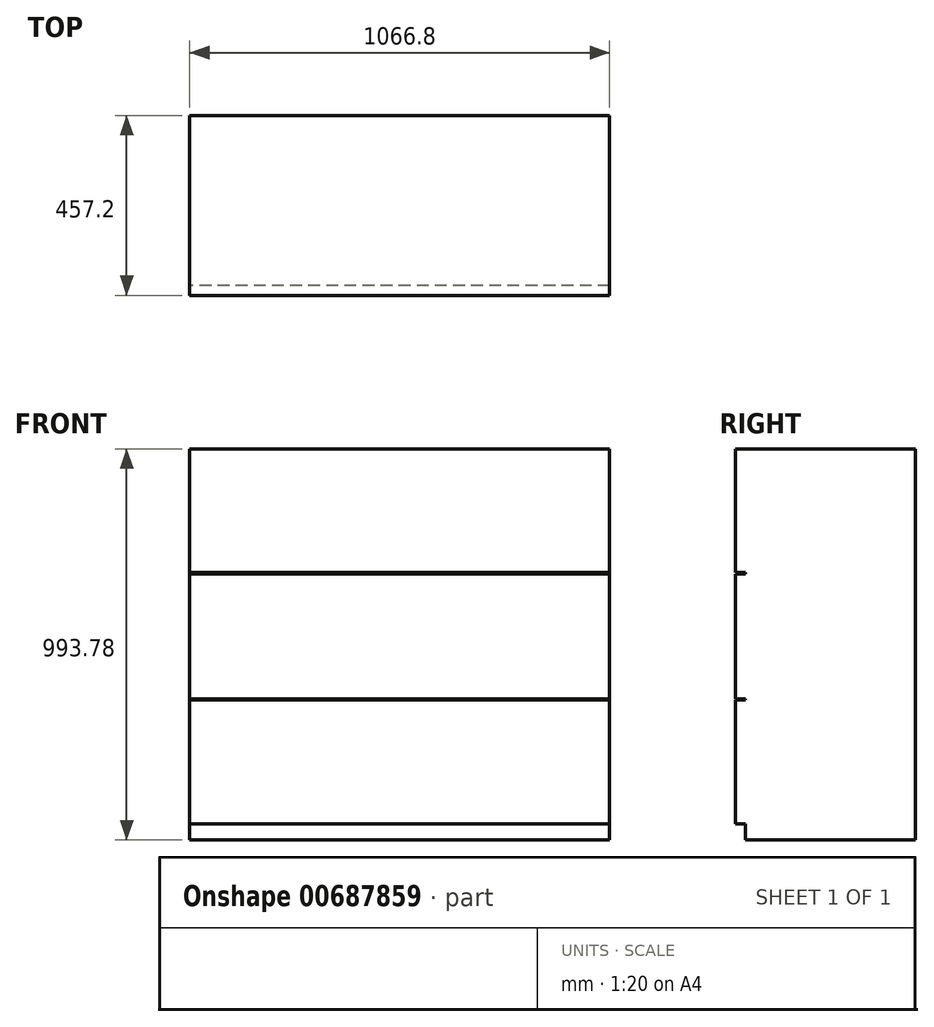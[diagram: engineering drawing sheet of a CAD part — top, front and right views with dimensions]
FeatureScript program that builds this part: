
annotation { "Feature Type Name" : "Feature", "Feature Type Description" : "" }
export const myFeature = defineFeature(function(context is Context, id is Id, definition is map)
    precondition{}
    {
        {
            var Q0;
            Q0=qCreatedBy(makeId("Front.planeOp"),FACE);
            var sketch = newSketch(context, id + "F0", { "sketchPlane" : qUnion([Q0])});
            skLineSegment(sketch, "E0.bottom", {"start": v(533.4, 496.89) * mm, "end": v(-533.4, 496.89) * mm});
            skLineSegment(sketch, "E0.top", {"start": v(533.4, -496.89) * mm, "end": v(-533.4, -496.89) * mm});
            skLineSegment(sketch, "E0.left", {"start": v(533.4, 496.89) * mm, "end": v(533.4, -496.89) * mm});
            skLineSegment(sketch, "E0.right", {"start": v(-533.4, 496.89) * mm, "end": v(-533.4, -496.89) * mm});
            skPoint(sketch, "E0.middle", {"position": v(0, 0) * mm});
            skSolve(sketch);
        }
        {
            var Q0;
            Q0=makeQuery(id+"F0.imprint","IMPRINT",FACE,{"disambiguationData":[TD([[makeQuery(id+"F0.imprint","IMPRINT",EDGE,{"derivedFrom":sQuery(id+"F0.wireOp",EDGE,"E0.bottom")}),1.0]])]});
            extrude(context, id + "F1", {"entities" : qUnion([Q0]), "depth" : 457.2 * mm, "offsetDistance" : 25.4 * mm});
        }
        {
            var Q0;
            Q0=makeQuery(id+"F1.opExtrude","CAP_FACE",FACE,{"disambiguationData":[OSD([sQuery(id+"F0.wireOp",EDGE,"E0.bottom"),sQuery(id+"F0.wireOp",EDGE,"E0.top"),sQuery(id+"F0.wireOp",EDGE,"E0.left"),sQuery(id+"F0.wireOp",EDGE,"E0.right")])],"isStart":false});
            var sketch = newSketch(context, id + "F2", { "sketchPlane" : qUnion([Q0])});
            skLineSegment(sketch, "E1.bottom", {"start": v(-533.4, -496.89) * mm, "end": v(533.4, -496.89) * mm});
            skLineSegment(sketch, "E1.top", {"start": v(-533.4, -455.74) * mm, "end": v(533.4, -455.74) * mm});
            skLineSegment(sketch, "E1.left", {"start": v(-533.4, -496.89) * mm, "end": v(-533.4, -455.74) * mm});
            skLineSegment(sketch, "E1.right", {"start": v(533.4, -496.89) * mm, "end": v(533.4, -455.74) * mm});
            skLineSegment(sketch, "E2", {"start": v(-533.4, -455.74) * mm, "end": v(-533.4, -141.41) * mm});
            skLineSegment(sketch, "E3.bottom", {"start": v(-533.4, -141.41) * mm, "end": v(533.4, -141.41) * mm});
            skLineSegment(sketch, "E3.top", {"start": v(-533.4, -138.24) * mm, "end": v(533.4, -138.24) * mm});
            skLineSegment(sketch, "E3.left", {"start": v(-533.4, -141.41) * mm, "end": v(-533.4, -138.24) * mm});
            skLineSegment(sketch, "E3.right", {"start": v(533.4, -141.41) * mm, "end": v(533.4, -138.24) * mm});
            skLineSegment(sketch, "E4", {"start": v(-533.4, 496.89) * mm, "end": v(-533.4, 182.56) * mm});
            skLineSegment(sketch, "E5.bottom", {"start": v(-533.4, 182.56) * mm, "end": v(533.4, 182.56) * mm});
            skLineSegment(sketch, "E5.top", {"start": v(-533.4, 179.39) * mm, "end": v(533.4, 179.39) * mm});
            skLineSegment(sketch, "E5.left", {"start": v(-533.4, 182.56) * mm, "end": v(-533.4, 179.39) * mm});
            skLineSegment(sketch, "E5.right", {"start": v(533.4, 182.56) * mm, "end": v(533.4, 179.39) * mm});
            skSolve(sketch);
        }
        {
            var Q0;
            Q0=makeQuery(id+"F2.imprint","IMPRINT",FACE,{"disambiguationData":[TD([[makeQuery(id+"F2.imprint","IMPRINT",EDGE,{"derivedFrom":sQuery(id+"F2.wireOp",EDGE,"E5.bottom")}),-1.0]])]});
            var Q1;
            Q1=makeQuery(id+"F2.imprint","IMPRINT",FACE,{"disambiguationData":[TD([[makeQuery(id+"F2.imprint","IMPRINT",EDGE,{"derivedFrom":sQuery(id+"F2.wireOp",EDGE,"E3.bottom")}),1.0]])]});
            var Q2;
            Q2=makeQuery(id+"F2.imprint","IMPRINT",FACE,{"disambiguationData":[TD([[makeQuery(id+"F2.imprint","IMPRINT",EDGE,{"derivedFrom":sQuery(id+"F2.wireOp",EDGE,"E1.bottom")}),-1.0]])]});
            extrude(context, id + "F3", {"entities" : qUnion([Q0, Q1, Q2]), "operationType" : NewBodyOperationType.REMOVE, "oppositeDirection" : true, "depth" : 25.4 * mm, "offsetDistance" : 25.4 * mm});
        }
    });
